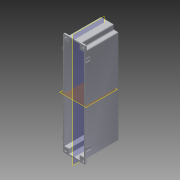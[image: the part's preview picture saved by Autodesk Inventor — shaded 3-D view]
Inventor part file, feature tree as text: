
AUTODESK INVENTOR PART (.ipt)
format: ipt  version: 2015 (Build 190159000, 159)  size: 212,992 bytes
history: native  units: mm
features: reference x14, sketch x5, extrude x4, plane x2, mirror x2, fillet x2, revolve x1, shell x1
ambient origin geometry x8: Origin, YZ Plane, XZ Plane, XY Plane, X Axis, Y Axis, Z Axis, Center Point
bodies: Solid1 (feature_tree)
feature tree (31):
  extrude  "Extrusion1"  Depth=235.0mm
  extrude  "Extrusion2"  Depth=3.0mm
  revolve  "Revolution1"  Angle=90.0deg
  plane  "Work Plane1"
  plane  "Work Plane2"
  mirror  "Mirror1"
  mirror  "Mirror2"
  extrude  "Extrusion3"  Depth=10.4mm
  shell  "Shell1"  Thickness=75.0mm
  extrude  "Extrusion4"  Depth=2.0mm
  fillet  "Fillet1"  Radius=2.0mm
  fillet  "Fillet2"  [1 undecoded]
  sketch  "Sketch1"  dims[d0=51.0mm d1=235.0mm]
  sketch  "Sketch2"  dims[d2=75.0mm d3=0.0mm d4=3.0mm]
  reference  "Reference1"
  reference  "Reference2"
  reference  "Reference3"
  reference  "Reference4"
  reference  "Reference5"
  reference  "Reference6"
  sketch  "Sketch3"  dims[d5=10.0mm d6=0.0mm d7=90.0deg]
  sketch  "Sketch4"  dims[d8=10.4mm d9=10.4mm d10=75.0mm d11=0.0mm]
  reference  "Reference7"
  reference  "Reference8"
  reference  "Reference9"
  reference  "Reference10"
  sketch  "Sketch5"  dims[d12=3.0mm d13=0.0mm d14=2.0mm d15=2.0mm]
  reference  "Reference11"
  reference  "Reference12"
  reference  "Reference13"
  reference  "Reference14"
note: 1 required parameter value undecoded (feature->parameter linkage not recoverable at this tier; creation-order binding heuristic only, values carry confidence <= 0.55)
